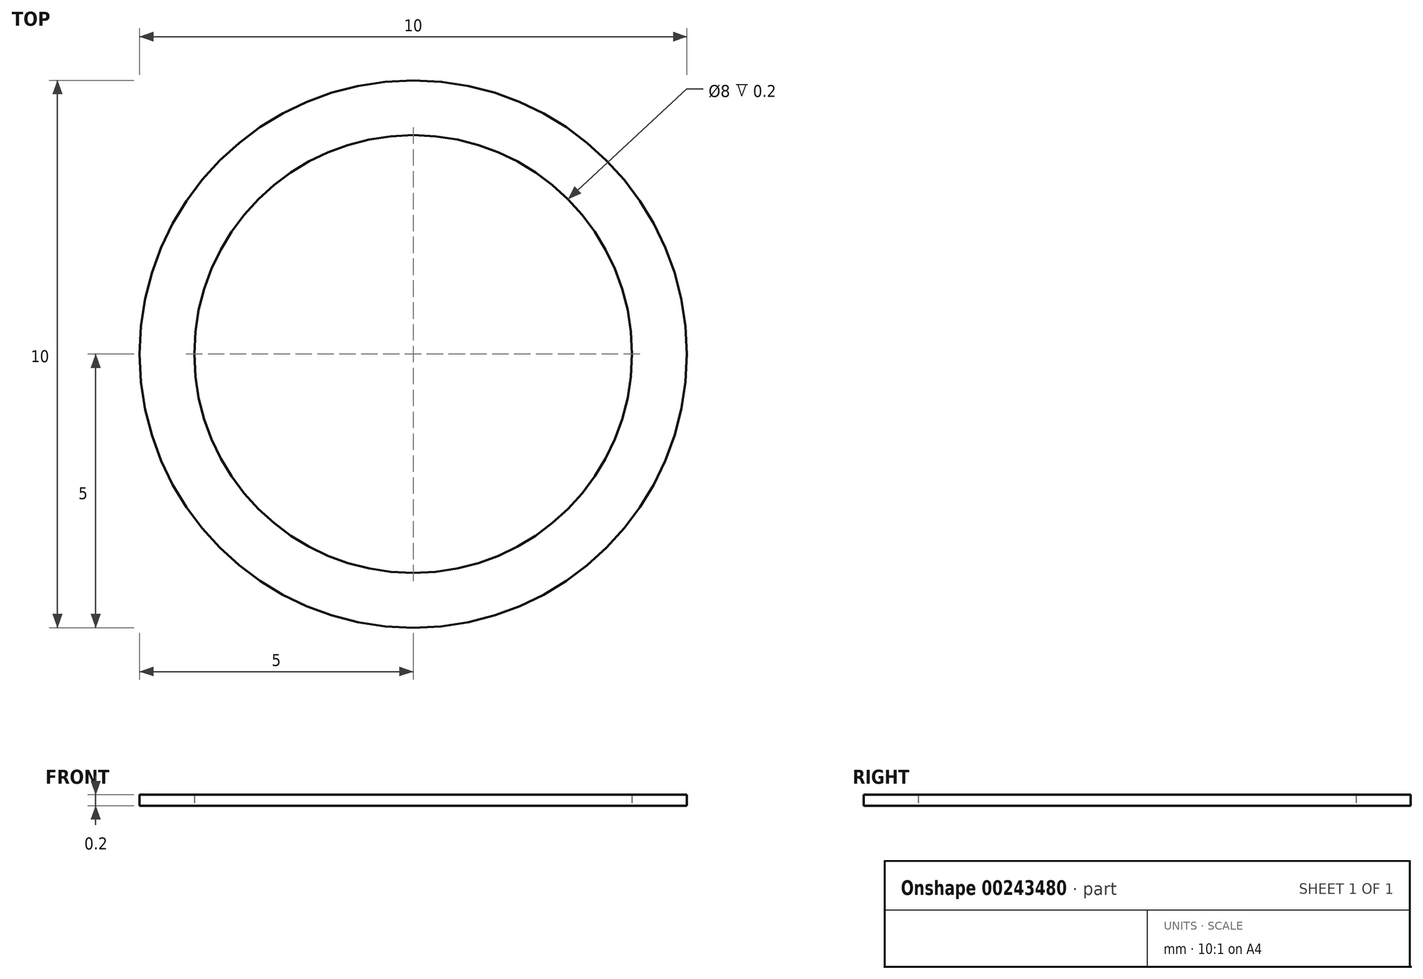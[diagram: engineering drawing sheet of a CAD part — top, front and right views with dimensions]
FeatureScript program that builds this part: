
annotation { "Feature Type Name" : "Feature", "Feature Type Description" : "" }
export const myFeature = defineFeature(function(context is Context, id is Id, definition is map)
    precondition{}
    {
        {
            var Q0;
            Q0=qCreatedBy(makeId("Top.planeOp"),FACE);
            var sketch = newSketch(context, id + "F0", { "sketchPlane" : qUnion([Q0])});
            skCircle(sketch, "E0", {"center": v(0, 0) * mm, "radius": 4 * mm});
            skCircle(sketch, "E1", {"center": v(0, 0) * mm, "radius": 5 * mm});
            skSolve(sketch);
        }
        {
            var Q0;
            Q0 = qSketchRegion(id + "F0", true);
            extrude(context, id + "F1", {"entities" : qUnion([Q0]), "depth" : 0.2 * mm, "offsetDistance" : 25 * mm});
        }
    });
